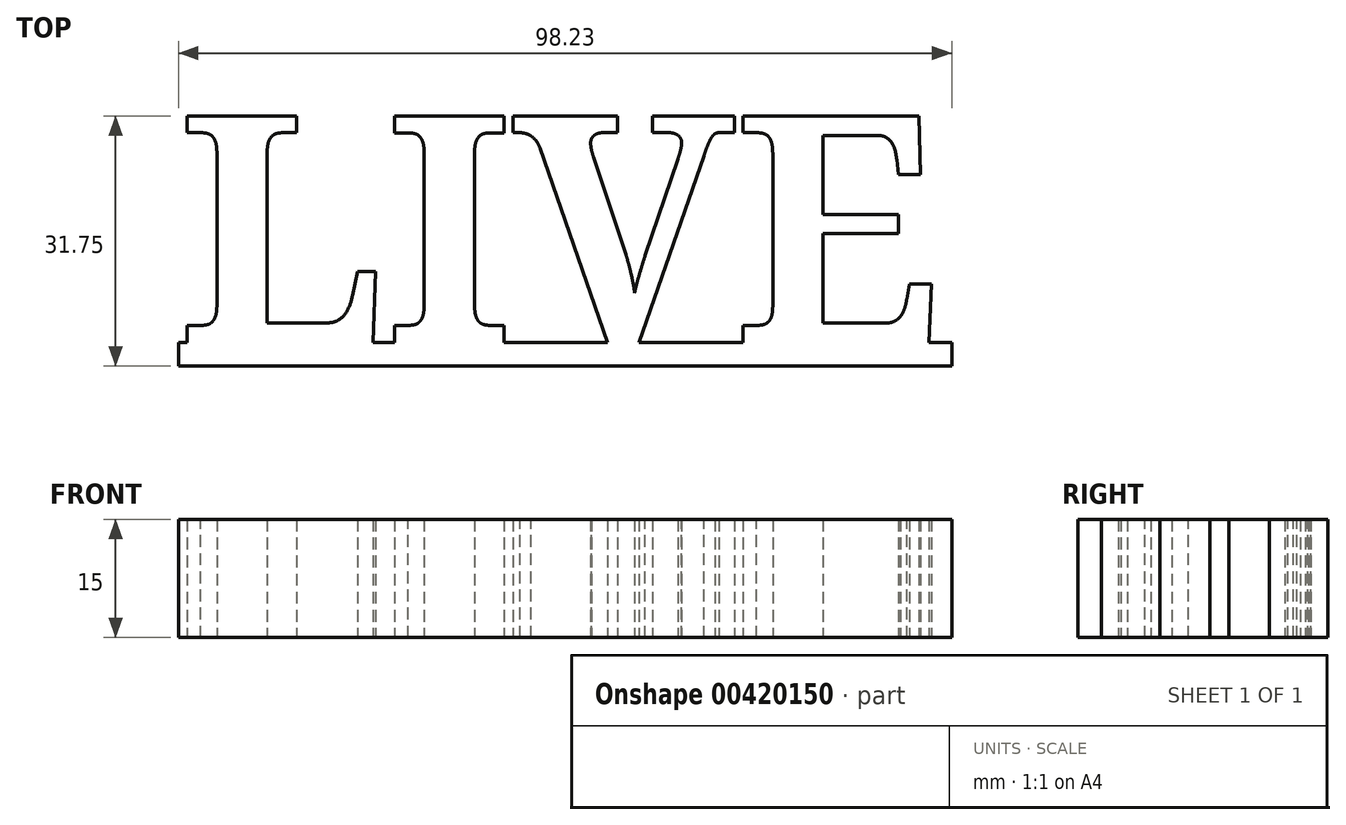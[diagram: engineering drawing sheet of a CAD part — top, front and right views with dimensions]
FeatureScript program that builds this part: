
annotation { "Feature Type Name" : "Feature", "Feature Type Description" : "" }
export const myFeature = defineFeature(function(context is Context, id is Id, definition is map)
    precondition{}
    {
        {
            var Q0;
            Q0=qCreatedBy(makeId("Top.planeOp"),FACE);
            var sketch = newSketch(context, id + "F0", { "sketchPlane" : qUnion([Q0])});
            skText(sketch, "E0", { "text": "LIVE", "fontName": "NotoSerif-Bold.ttf"});
            skLineSegment(sketch, "E1", {"start": v(0, 0) * mm, "end": v(24.92, 0) * mm});
            skLineSegment(sketch, "E2", {"start": v(0, 0) * mm, "end": v(98.23, 0) * mm});
            skLineSegment(sketch, "E3", {"start": v(98.23, -3) * mm, "end": v(0, -3) * mm});
            skLineSegment(sketch, "E4", {"start": v(0, -3) * mm, "end": v(0, 0) * mm});
            skLineSegment(sketch, "E5", {"start": v(98.23, -3) * mm, "end": v(98.23, 0) * mm});
            const initialGuessF0  = {"E0": [0, 0, 1, 0, 0.029]};
            skSetInitialGuess(sketch, initialGuessF0);
            skSolve(sketch);
        }
        {
            var Q0;
            Q0=qSketchRegion(id+"F0",true);
            extrude(context, id + "F1", {"entities" : qUnion([Q0]), "depth" : 15 * mm});
        }
    });
